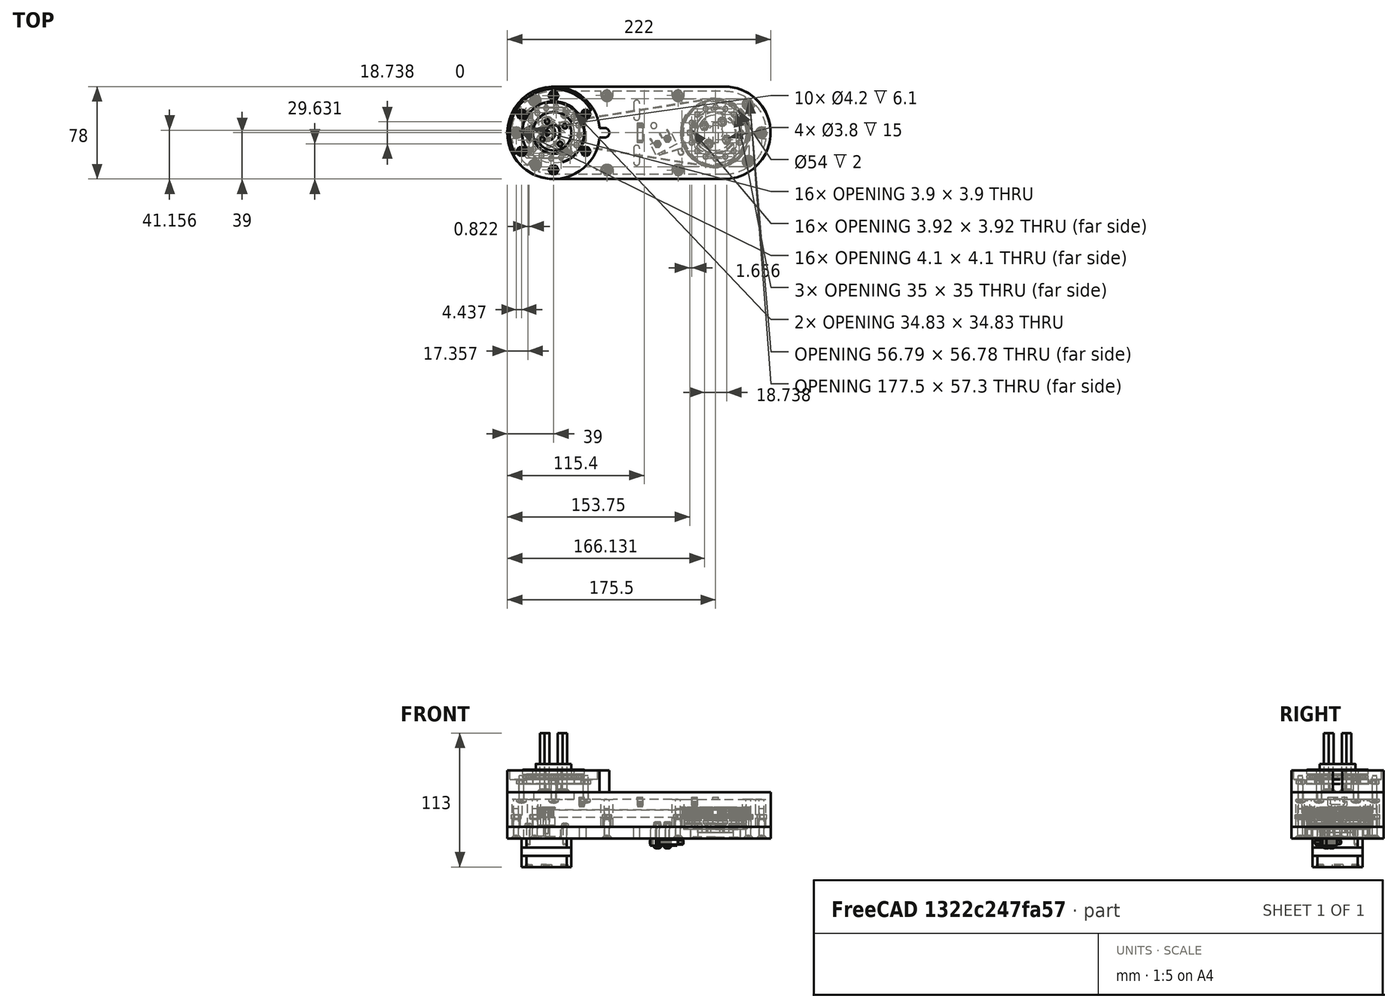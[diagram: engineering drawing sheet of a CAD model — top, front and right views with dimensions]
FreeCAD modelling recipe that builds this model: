
FCSTD DOCUMENT  (FreeCAD 0.19R)
Label: Arm2_a2p
License: All rights reserved
LicenseURL: http://en.wikipedia.org/wiki/All_rights_reserved
objects: Part::FeaturePython×66, App::FeaturePython×48, Spreadsheet::Sheet×2, App::DocumentObjectGroup×1
note: 66 computed .brp shape members not serialized (recipe doc carries the construction recipe); baked Part::Feature solids carry a one-line shape summary decoded from their .brp

FEATURE [Part::FeaturePython] b_Arm2_cover_modified_001_  label="Arm2_cover_modified_001"  # a2plus imported part (geometry in sourceFile) (typed FeaturePython)
  Placement = pos=(0,0,0) rot=(1,0,0;1.5708rad)
  a2p_Version = V0.1
  fixedPosition = true
  objectType = a2pPart
  sourceFile = ./Arm2_cover_modified.FCStd
  subassemblyImport = false
  timeLastImport = 1.62057e+09
  updateColors = true
FEATURE [Part::FeaturePython] b_Thrust_bearing_511071_001_  label="Thrust_bearing_511071_001"  # a2plus imported part (geometry in sourceFile) (typed FeaturePython)
  Placement = pos=(-7.5,3.014e-12,8) rot=(1,0,0;1.5708rad)
  a2p_Version = V0.1
  fixedPosition = false
  objectType = a2pPart
  sourceFile = ./Thrust_bearing_51107.step
  subassemblyImport = false
  timeLastImport = 1.62049e+09
  updateColors = true
FEATURE [App::FeaturePython] circularEdge_002  label="circularEdge_002__Arm2_cover_modified_001"  # a2plus constraint (typed FeaturePython)
  Object1 = b_Thrust_bearing_511071_001_
  Object2 = b_Arm2_cover_modified_001_
  ParentTreeObject = -> b_Thrust_bearing_511071_001_
  SubElement1 = Edge18
  SubElement2 = Edge329
  Suppressed = false
  Type = circularEdge
  directionConstraint = 1
  lockRotation = false
  offset = 0
FEATURE [App::FeaturePython] circularEdge_002_mirror  label="circularEdge_002__Thrust_bearing_511071_001"  # a2plus constraint (typed FeaturePython)
  Object1 = b_Thrust_bearing_511071_001_
  Object2 = b_Arm2_cover_modified_001_
  ParentTreeObject = -> b_Arm2_cover_modified_001_
  SubElement1 = Edge18
  SubElement2 = Edge329
  Suppressed = false
  Type = circularEdge
  directionConstraint = 1
  lockRotation = false
  offset = 0
FEATURE [Part::FeaturePython] b_Stepper_NEMA17_l24mm_shaft_20mm1_001_  label="Stepper_NEMA17_l24mm_shaft_20mm1_001"  # a2plus imported part (geometry in sourceFile) (typed FeaturePython)
  Placement = pos=(-150,-3.93946e-07,-24) rot=(1,0,0;1.5708rad)
  a2p_Version = V0.1
  fixedPosition = false
  objectType = a2pPart
  sourceFile = ./Stepper_NEMA17_l24mm_shaft_20mm.step
  subassemblyImport = false
  timeLastImport = 1.62058e+09
  updateColors = true
FEATURE [App::FeaturePython] circularEdge_004  label="circularEdge_004__Arm2_cover_modified_001"  # a2plus constraint (typed FeaturePython)
  Object1 = b_Stepper_NEMA17_l24mm_shaft_20mm1_001_
  Object2 = b_Arm2_cover_modified_001_
  ParentTreeObject = -> b_Stepper_NEMA17_l24mm_shaft_20mm1_001_
  SubElement1 = Edge95
  SubElement2 = Edge24
  Suppressed = false
  Type = circularEdge
  directionConstraint = 0
  lockRotation = false
  offset = 0
FEATURE [App::FeaturePython] circularEdge_004_mirror  label="circularEdge_004__Stepper_NEMA17_l24mm_shaft_20mm1_001"  # a2plus constraint (typed FeaturePython)
  Object1 = b_Stepper_NEMA17_l24mm_shaft_20mm1_001_
  Object2 = b_Arm2_cover_modified_001_
  ParentTreeObject = -> b_Arm2_cover_modified_001_
  SubElement1 = Edge95
  SubElement2 = Edge24
  Suppressed = false
  Type = circularEdge
  directionConstraint = 0
  lockRotation = false
  offset = 0
FEATURE [App::FeaturePython] axisCoincident_001  label="axisCoincident_001__Arm2_cover_modified_001"  # a2plus constraint (typed FeaturePython)
  Object1 = b_Stepper_NEMA17_l24mm_shaft_20mm1_001_
  Object2 = b_Arm2_cover_modified_001_
  ParentTreeObject = -> b_Stepper_NEMA17_l24mm_shaft_20mm1_001_
  SubElement1 = Face40
  SubElement2 = Face44
  Suppressed = false
  Type = axial
  directionConstraint = 0
  lockRotation = false
FEATURE [App::FeaturePython] axisCoincident_001_mirror  label="axisCoincident_001__Stepper_NEMA17_l24mm_shaft_20mm1_001"  # a2plus constraint (typed FeaturePython)
  Object1 = b_Stepper_NEMA17_l24mm_shaft_20mm1_001_
  Object2 = b_Arm2_cover_modified_001_
  ParentTreeObject = -> b_Arm2_cover_modified_001_
  SubElement1 = Face40
  SubElement2 = Face44
  Suppressed = false
  Type = axial
  directionConstraint = 0
  lockRotation = false
FEATURE [Part::FeaturePython] b_Pulley_GT2_20t1_001_  label="Pulley_GT2-20t1_001"  # a2plus imported part (geometry in sourceFile) (typed FeaturePython)
  Placement = pos=(-209.577,47.8545,-1.09998) rot=(-0.402665,-0.647248,0.647248;2.37599rad)
  a2p_Version = V0.1
  fixedPosition = false
  objectType = a2pPart
  sourceFile = ./Pulley_GT2-20t.step
  subassemblyImport = false
  timeLastImport = 1.61956e+09
  updateColors = true
FEATURE [App::FeaturePython] axisCoincident_002  label="axisCoincident_002__Stepper_NEMA17_l24mm_shaft_20mm1_001"  # a2plus constraint (typed FeaturePython)
  Object1 = b_Pulley_GT2_20t1_001_
  Object2 = b_Stepper_NEMA17_l24mm_shaft_20mm1_001_
  ParentTreeObject = -> b_Pulley_GT2_20t1_001_
  SubElement1 = Face190
  SubElement2 = Face31
  Suppressed = false
  Type = axial
  directionConstraint = 1
  lockRotation = false
FEATURE [App::FeaturePython] axisCoincident_002_mirror  label="axisCoincident_002__Pulley_GT2-20t1_001"  # a2plus constraint (typed FeaturePython)
  Object1 = b_Pulley_GT2_20t1_001_
  Object2 = b_Stepper_NEMA17_l24mm_shaft_20mm1_001_
  ParentTreeObject = -> b_Stepper_NEMA17_l24mm_shaft_20mm1_001_
  SubElement1 = Face190
  SubElement2 = Face31
  Suppressed = false
  Type = axial
  directionConstraint = 1
  lockRotation = false
FEATURE [Part::FeaturePython] b_Belt_GT2_400mm_20_901_001_  label="Belt_GT2_400mm_20-901_001"  # a2plus imported part (geometry in sourceFile) (typed FeaturePython)
  Placement = pos=(-7.5,7.81778e-08,24.2) rot=(-1,0,0;1.5708rad)
  a2p_Version = V0.1
  fixedPosition = false
  objectType = a2pPart
  sourceFile = ./Belt_GT2_400mm_20-90.step
  subassemblyImport = false
  timeLastImport = 1.62058e+09
  updateColors = true
FEATURE [App::FeaturePython] axisCoincident_003  label="axisCoincident_003__Pulley_GT2-20t1_001"  # a2plus constraint (typed FeaturePython)
  Object1 = b_Belt_GT2_400mm_20_901_001_
  Object2 = b_Pulley_GT2_20t1_001_
  ParentTreeObject = -> b_Belt_GT2_400mm_20_901_001_
  SubElement1 = Face11
  SubElement2 = Face187
  Suppressed = false
  Type = axial
  directionConstraint = 0
  lockRotation = false
FEATURE [App::FeaturePython] axisCoincident_003_mirror  label="axisCoincident_003__Belt_GT2_400mm_20-901_001"  # a2plus constraint (typed FeaturePython)
  Object1 = b_Belt_GT2_400mm_20_901_001_
  Object2 = b_Pulley_GT2_20t1_001_
  ParentTreeObject = -> b_Pulley_GT2_20t1_001_
  SubElement1 = Face11
  SubElement2 = Face187
  Suppressed = false
  Type = axial
  directionConstraint = 0
  lockRotation = false
FEATURE [Part::FeaturePython] b_Arm2_modified_001_  label="Arm2_modified_001"  # a2plus imported part (geometry in sourceFile) (typed FeaturePython)
  Placement = pos=(0,-4.78538e-07,39) rot=(-1,0,0;1.5708rad)
  a2p_Version = V0.1
  fixedPosition = false
  objectType = a2pPart
  sourceFile = ./Arm2_modified.FCStd
  subassemblyImport = false
  timeLastImport = 1.62049e+09
  updateColors = true
FEATURE [Part::FeaturePython] b_Cable_routing_clamp_16_8_4_5_001_  label="Cable_routing_clamp_16*8*4.5_001"  # a2plus imported part (geometry in sourceFile) (typed FeaturePython)
  Placement = pos=(-122.4,-8.1,27) rot=(0.57735,0.57735,0.57735;2.0944rad)
  a2p_Version = V0.1
  fixedPosition = false
  objectType = a2pPart
  sourceFile = ./Cable_routing_clamp_16*8*4.5.FCStd
  subassemblyImport = false
  timeLastImport = 1.62049e+09
  updateColors = true
FEATURE [App::FeaturePython] circularEdge_006  label="circularEdge_006__Arm2_cover_modified_001"  # a2plus constraint (typed FeaturePython)
  Object1 = b_Arm2_modified_001_
  Object2 = b_Arm2_cover_modified_001_
  ParentTreeObject = -> b_Arm2_modified_001_
  SubElement1 = Edge125
  SubElement2 = Edge114
  Suppressed = false
  Type = circularEdge
  directionConstraint = 0
  lockRotation = true
  offset = 0
FEATURE [App::FeaturePython] circularEdge_006_mirror  label="circularEdge_006__Arm2_modified_001"  # a2plus constraint (typed FeaturePython)
  Object1 = b_Arm2_modified_001_
  Object2 = b_Arm2_cover_modified_001_
  ParentTreeObject = -> b_Arm2_cover_modified_001_
  SubElement1 = Edge125
  SubElement2 = Edge114
  Suppressed = false
  Type = circularEdge
  directionConstraint = 0
  lockRotation = true
  offset = 0
FEATURE [App::FeaturePython] planeCoincident_002  label="planeCoincident_002__Arm2_modified_001"  # a2plus constraint (typed FeaturePython)
  Object1 = b_Cable_routing_clamp_16_8_4_5_001_
  Object2 = b_Arm2_modified_001_
  ParentTreeObject = -> b_Cable_routing_clamp_16_8_4_5_001_
  SubElement1 = Face9
  SubElement2 = Face77
  Suppressed = false
  Type = plane
  directionConstraint = 1
  offset = 0
FEATURE [App::FeaturePython] planeCoincident_002_mirror  label="planeCoincident_002__Cable_routing_clamp_16*8*4.5_001"  # a2plus constraint (typed FeaturePython)
  Object1 = b_Cable_routing_clamp_16_8_4_5_001_
  Object2 = b_Arm2_modified_001_
  ParentTreeObject = -> b_Arm2_modified_001_
  SubElement1 = Face9
  SubElement2 = Face77
  Suppressed = false
  Type = plane
  directionConstraint = 1
  offset = 0
FEATURE [App::FeaturePython] planeCoincident_003  label="planeCoincident_003__Arm2_modified_001"  # a2plus constraint (typed FeaturePython)
  Object1 = b_Cable_routing_clamp_16_8_4_5_001_
  Object2 = b_Arm2_modified_001_
  ParentTreeObject = -> b_Cable_routing_clamp_16_8_4_5_001_
  SubElement1 = Face5
  SubElement2 = Face166
  Suppressed = false
  Type = plane
  directionConstraint = 0
  offset = 0
FEATURE [App::FeaturePython] planeCoincident_003_mirror  label="planeCoincident_003__Cable_routing_clamp_16*8*4.5_001"  # a2plus constraint (typed FeaturePython)
  Object1 = b_Cable_routing_clamp_16_8_4_5_001_
  Object2 = b_Arm2_modified_001_
  ParentTreeObject = -> b_Arm2_modified_001_
  SubElement1 = Face5
  SubElement2 = Face166
  Suppressed = false
  Type = plane
  directionConstraint = 0
  offset = 0
FEATURE [App::FeaturePython] planeCoincident_004  label="planeCoincident_004__Arm2_modified_001"  # a2plus constraint (typed FeaturePython)
  Object1 = b_Cable_routing_clamp_16_8_4_5_001_
  Object2 = b_Arm2_modified_001_
  ParentTreeObject = -> b_Cable_routing_clamp_16_8_4_5_001_
  SubElement1 = Face24
  SubElement2 = Face76
  Suppressed = false
  Type = plane
  directionConstraint = 0
  offset = 0
FEATURE [App::FeaturePython] planeCoincident_004_mirror  label="planeCoincident_004__Cable_routing_clamp_16*8*4.5_001"  # a2plus constraint (typed FeaturePython)
  Object1 = b_Cable_routing_clamp_16_8_4_5_001_
  Object2 = b_Arm2_modified_001_
  ParentTreeObject = -> b_Arm2_modified_001_
  SubElement1 = Face24
  SubElement2 = Face76
  Suppressed = false
  Type = plane
  directionConstraint = 0
  offset = 0
FEATURE [Part::FeaturePython] b_Cable_routing_clamp_16_8_4_5_001_001  label="Cable_routing_clamp_16*8*4.5_002"  # a2plus imported part (geometry in sourceFile) (typed FeaturePython)
  Placement = pos=(-73.4,-8.1,27) rot=(0.57735,0.57735,0.57735;2.0944rad)
  a2p_Version = V0.1
  fixedPosition = false
  objectType = a2pPart
  sourceFile = ./Cable_routing_clamp_16*8*4.5.FCStd
  subassemblyImport = false
  timeLastImport = 1.62049e+09
  updateColors = true
FEATURE [App::FeaturePython] planeCoincident_005  label="planeCoincident_005__Arm2_modified_001"  # a2plus constraint (typed FeaturePython)
  Object1 = b_Cable_routing_clamp_16_8_4_5_001_001
  Object2 = b_Arm2_modified_001_
  ParentTreeObject = -> b_Cable_routing_clamp_16_8_4_5_001_001
  SubElement1 = Face24
  SubElement2 = Face82
  Suppressed = false
  Type = plane
  directionConstraint = 0
  offset = 0
FEATURE [App::FeaturePython] planeCoincident_005_mirror  label="planeCoincident_005__Cable_routing_clamp_16*8*4.5_002"  # a2plus constraint (typed FeaturePython)
  Object1 = b_Cable_routing_clamp_16_8_4_5_001_001
  Object2 = b_Arm2_modified_001_
  ParentTreeObject = -> b_Arm2_modified_001_
  SubElement1 = Face24
  SubElement2 = Face82
  Suppressed = false
  Type = plane
  directionConstraint = 0
  offset = 0
FEATURE [App::FeaturePython] planeCoincident_006  label="planeCoincident_006__Arm2_modified_001"  # a2plus constraint (typed FeaturePython)
  Object1 = b_Cable_routing_clamp_16_8_4_5_001_001
  Object2 = b_Arm2_modified_001_
  ParentTreeObject = -> b_Cable_routing_clamp_16_8_4_5_001_001
  SubElement1 = Face9
  SubElement2 = Face83
  Suppressed = false
  Type = plane
  directionConstraint = 1
  offset = 0
FEATURE [App::FeaturePython] planeCoincident_006_mirror  label="planeCoincident_006__Cable_routing_clamp_16*8*4.5_002"  # a2plus constraint (typed FeaturePython)
  Object1 = b_Cable_routing_clamp_16_8_4_5_001_001
  Object2 = b_Arm2_modified_001_
  ParentTreeObject = -> b_Arm2_modified_001_
  SubElement1 = Face9
  SubElement2 = Face83
  Suppressed = false
  Type = plane
  directionConstraint = 1
  offset = 0
FEATURE [App::FeaturePython] planeCoincident_007  label="planeCoincident_007__Cable_routing_clamp_16*8*4.5_001"  # a2plus constraint (typed FeaturePython)
  Object1 = b_Cable_routing_clamp_16_8_4_5_001_001
  Object2 = b_Cable_routing_clamp_16_8_4_5_001_
  ParentTreeObject = -> b_Cable_routing_clamp_16_8_4_5_001_001
  SubElement1 = Face13
  SubElement2 = Face13
  Suppressed = false
  Type = plane
  directionConstraint = 0
  offset = 0
FEATURE [App::FeaturePython] planeCoincident_007_mirror  label="planeCoincident_007__Cable_routing_clamp_16*8*4.5_002"  # a2plus constraint (typed FeaturePython)
  Object1 = b_Cable_routing_clamp_16_8_4_5_001_001
  Object2 = b_Cable_routing_clamp_16_8_4_5_001_
  ParentTreeObject = -> b_Cable_routing_clamp_16_8_4_5_001_
  SubElement1 = Face13
  SubElement2 = Face13
  Suppressed = false
  Type = plane
  directionConstraint = 0
  offset = 0
FEATURE [Part::FeaturePython] b_Cable_routing_clamp_16_8_4_5_001_002  label="Cable_routing_clamp_16*8*4.5_003"  # a2plus imported part (geometry in sourceFile) (typed FeaturePython)
  Placement = pos=(-27.4,-8.1,27) rot=(0.57735,0.57735,0.57735;2.0944rad)
  a2p_Version = V0.1
  fixedPosition = false
  objectType = a2pPart
  sourceFile = ./Cable_routing_clamp_16*8*4.5.FCStd
  subassemblyImport = false
  timeLastImport = 1.62049e+09
  updateColors = true
FEATURE [App::FeaturePython] planeCoincident_008  label="planeCoincident_008__Arm2_modified_001"  # a2plus constraint (typed FeaturePython)
  Object1 = b_Cable_routing_clamp_16_8_4_5_001_002
  Object2 = b_Arm2_modified_001_
  ParentTreeObject = -> b_Cable_routing_clamp_16_8_4_5_001_002
  SubElement1 = Face9
  SubElement2 = Face87
  Suppressed = false
  Type = plane
  directionConstraint = 1
  offset = 0
FEATURE [App::FeaturePython] planeCoincident_008_mirror  label="planeCoincident_008__Cable_routing_clamp_16*8*4.5_003"  # a2plus constraint (typed FeaturePython)
  Object1 = b_Cable_routing_clamp_16_8_4_5_001_002
  Object2 = b_Arm2_modified_001_
  ParentTreeObject = -> b_Arm2_modified_001_
  SubElement1 = Face9
  SubElement2 = Face87
  Suppressed = false
  Type = plane
  directionConstraint = 1
  offset = 0
FEATURE [App::FeaturePython] planeCoincident_009  label="planeCoincident_009__Arm2_modified_001"  # a2plus constraint (typed FeaturePython)
  Object1 = b_Cable_routing_clamp_16_8_4_5_001_002
  Object2 = b_Arm2_modified_001_
  ParentTreeObject = -> b_Cable_routing_clamp_16_8_4_5_001_002
  SubElement1 = Face24
  SubElement2 = Face86
  Suppressed = false
  Type = plane
  directionConstraint = 0
  offset = 0
FEATURE [App::FeaturePython] planeCoincident_009_mirror  label="planeCoincident_009__Cable_routing_clamp_16*8*4.5_003"  # a2plus constraint (typed FeaturePython)
  Object1 = b_Cable_routing_clamp_16_8_4_5_001_002
  Object2 = b_Arm2_modified_001_
  ParentTreeObject = -> b_Arm2_modified_001_
  SubElement1 = Face24
  SubElement2 = Face86
  Suppressed = false
  Type = plane
  directionConstraint = 0
  offset = 0
FEATURE [App::FeaturePython] planeCoincident_010  label="planeCoincident_010__Cable_routing_clamp_16*8*4.5_001"  # a2plus constraint (typed FeaturePython)
  Object1 = b_Cable_routing_clamp_16_8_4_5_001_002
  Object2 = b_Cable_routing_clamp_16_8_4_5_001_
  ParentTreeObject = -> b_Cable_routing_clamp_16_8_4_5_001_002
  SubElement1 = Face13
  SubElement2 = Face13
  Suppressed = false
  Type = plane
  directionConstraint = 0
  offset = 0
FEATURE [App::FeaturePython] planeCoincident_010_mirror  label="planeCoincident_010__Cable_routing_clamp_16*8*4.5_003"  # a2plus constraint (typed FeaturePython)
  Object1 = b_Cable_routing_clamp_16_8_4_5_001_002
  Object2 = b_Cable_routing_clamp_16_8_4_5_001_
  ParentTreeObject = -> b_Cable_routing_clamp_16_8_4_5_001_
  SubElement1 = Face13
  SubElement2 = Face13
  Suppressed = false
  Type = plane
  directionConstraint = 0
  offset = 0
FEATURE [Part::FeaturePython] b_J2_coupler_modified_001_  label="J2_coupler_modified_001"  # a2plus imported part (geometry in sourceFile) (typed FeaturePython)
  Placement = pos=(-144,7.32498e-07,39) rot=(0.377965,0.654654,0.654654;2.41886rad)
  a2p_Version = V0.1
  fixedPosition = false
  objectType = a2pPart
  sourceFile = ./J2_coupler_modified.FCStd
  subassemblyImport = false
  timeLastImport = 1.62049e+09
  updateColors = true
FEATURE [App::FeaturePython] circularEdge_007  label="circularEdge_007__Arm2_modified_001"  # a2plus constraint (typed FeaturePython)
  Object1 = b_J2_coupler_modified_001_
  Object2 = b_Arm2_modified_001_
  ParentTreeObject = -> b_J2_coupler_modified_001_
  SubElement1 = Edge11
  SubElement2 = Edge345
  Suppressed = false
  Type = circularEdge
  directionConstraint = 1
  lockRotation = false
  offset = 0
FEATURE [App::FeaturePython] circularEdge_007_mirror  label="circularEdge_007__J2_coupler_modified_001"  # a2plus constraint (typed FeaturePython)
  Object1 = b_J2_coupler_modified_001_
  Object2 = b_Arm2_modified_001_
  ParentTreeObject = -> b_Arm2_modified_001_
  SubElement1 = Edge11
  SubElement2 = Edge345
  Suppressed = false
  Type = circularEdge
  directionConstraint = 1
  lockRotation = false
  offset = 0
FEATURE [App::FeaturePython] axisCoincident_004  label="axisCoincident_004__Arm2_modified_001"  # a2plus constraint (typed FeaturePython)
  Object1 = b_J2_coupler_modified_001_
  Object2 = b_Arm2_modified_001_
  ParentTreeObject = -> b_J2_coupler_modified_001_
  SubElement1 = Edge138
  SubElement2 = Edge327
  Suppressed = false
  Type = axial
  directionConstraint = 1
  lockRotation = false
FEATURE [App::FeaturePython] axisCoincident_004_mirror  label="axisCoincident_004__J2_coupler_modified_001"  # a2plus constraint (typed FeaturePython)
  Object1 = b_J2_coupler_modified_001_
  Object2 = b_Arm2_modified_001_
  ParentTreeObject = -> b_Arm2_modified_001_
  SubElement1 = Edge138
  SubElement2 = Edge327
  Suppressed = false
  Type = axial
  directionConstraint = 1
  lockRotation = false
FEATURE [Part::FeaturePython] b_Thrust_bearing_511071_001_001  label="Thrust_bearing_511071_002"  # a2plus imported part (geometry in sourceFile) (typed FeaturePython)
  Placement = pos=(-144,8.98781e-07,58) rot=(-0.978852,-0.144653,0.144653;1.59217rad)
  a2p_Version = V0.1
  fixedPosition = false
  objectType = a2pPart
  sourceFile = ./Thrust_bearing_51107.step
  subassemblyImport = false
  timeLastImport = 1.62049e+09
  updateColors = true
FEATURE [App::FeaturePython] planeCoincident_014  label="planeCoincident_014__J2_coupler_modified_001"  # a2plus constraint (typed FeaturePython)
  Object1 = b_Thrust_bearing_511071_001_001
  Object2 = b_J2_coupler_modified_001_
  ParentTreeObject = -> b_Thrust_bearing_511071_001_001
  SubElement1 = Face13
  SubElement2 = Face99
  Suppressed = false
  Type = plane
  directionConstraint = 1
  offset = 0
FEATURE [App::FeaturePython] planeCoincident_014_mirror  label="planeCoincident_014__Thrust_bearing_511071_002"  # a2plus constraint (typed FeaturePython)
  Object1 = b_Thrust_bearing_511071_001_001
  Object2 = b_J2_coupler_modified_001_
  ParentTreeObject = -> b_J2_coupler_modified_001_
  SubElement1 = Face13
  SubElement2 = Face99
  Suppressed = false
  Type = plane
  directionConstraint = 1
  offset = 0
FEATURE [App::FeaturePython] axisCoincident_005  label="axisCoincident_005__J2_coupler_modified_001"  # a2plus constraint (typed FeaturePython)
  Object1 = b_Thrust_bearing_511071_001_001
  Object2 = b_J2_coupler_modified_001_
  ParentTreeObject = -> b_Thrust_bearing_511071_001_001
  SubElement1 = Face2
  SubElement2 = Face88
  Suppressed = false
  Type = axial
  directionConstraint = 0
  lockRotation = false
FEATURE [App::FeaturePython] axisCoincident_005_mirror  label="axisCoincident_005__Thrust_bearing_511071_002"  # a2plus constraint (typed FeaturePython)
  Object1 = b_Thrust_bearing_511071_001_001
  Object2 = b_J2_coupler_modified_001_
  ParentTreeObject = -> b_J2_coupler_modified_001_
  SubElement1 = Face2
  SubElement2 = Face88
  Suppressed = false
  Type = axial
  directionConstraint = 0
  lockRotation = false
FEATURE [Part::FeaturePython] b_Switch_endstop1_001_  label="Switch_endstop1_001"  # a2plus imported part (geometry in sourceFile) (typed FeaturePython)
  Placement = pos=(-51.2411,-9.55473,-7.65812e-08) rot=(0.970296,0.241922,0;3.14159rad)
  a2p_Version = V0.1
  fixedPosition = false
  objectType = a2pPart
  sourceFile = ./Switch_endstop.step
  subassemblyImport = false
  timeLastImport = 1598970250
  updateColors = true
FEATURE [App::FeaturePython] circularEdge_008  label="circularEdge_008__Arm2_cover_modified_001"  # a2plus constraint (typed FeaturePython)
  Object1 = b_Switch_endstop1_001_
  Object2 = b_Arm2_cover_modified_001_
  ParentTreeObject = -> b_Switch_endstop1_001_
  SubElement1 = Edge39
  SubElement2 = Edge71
  Suppressed = false
  Type = circularEdge
  directionConstraint = 1
  lockRotation = false
  offset = 0
FEATURE [App::FeaturePython] circularEdge_008_mirror  label="circularEdge_008__Switch_endstop1_001"  # a2plus constraint (typed FeaturePython)
  Object1 = b_Switch_endstop1_001_
  Object2 = b_Arm2_cover_modified_001_
  ParentTreeObject = -> b_Arm2_cover_modified_001_
  SubElement1 = Edge39
  SubElement2 = Edge71
  Suppressed = false
  Type = circularEdge
  directionConstraint = 1
  lockRotation = false
  offset = 0
FEATURE [App::FeaturePython] axisCoincident_006  label="axisCoincident_006__Arm2_cover_modified_001"  # a2plus constraint (typed FeaturePython)
  Object1 = b_Switch_endstop1_001_
  Object2 = b_Arm2_cover_modified_001_
  ParentTreeObject = -> b_Switch_endstop1_001_
  SubElement1 = Face10
  SubElement2 = Face64
  Suppressed = false
  Type = axial
  directionConstraint = 1
  lockRotation = false
FEATURE [App::FeaturePython] axisCoincident_006_mirror  label="axisCoincident_006__Switch_endstop1_001"  # a2plus constraint (typed FeaturePython)
  Object1 = b_Switch_endstop1_001_
  Object2 = b_Arm2_cover_modified_001_
  ParentTreeObject = -> b_Arm2_cover_modified_001_
  SubElement1 = Face10
  SubElement2 = Face64
  Suppressed = false
  Type = axial
  directionConstraint = 1
  lockRotation = false
FEATURE [Part::FeaturePython] Nut  label="M4-Nut"  # Fasteners workbench fastener (typed FeaturePython)
  Placement = pos=(-99,31.5,20) rot=(1,0,0;3.14159rad)
  baseObject = -> b_Arm2_modified_001_ [Edge461]
  diameter = 6
  invert = true
  matchOuter = false
  offset = 0
  thread = false
  type = 7
FEATURE [Part::FeaturePython] Nut001  label="M4-Nut001"  # Fasteners workbench fastener (typed FeaturePython)
  Placement = pos=(-159.75,27.2798,20) rot=(1,0,0;3.14159rad)
  baseObject = -> b_Arm2_modified_001_ [Edge485]
  diameter = 6
  invert = false
  matchOuter = false
  offset = 0
  thread = false
  type = 7
FEATURE [Part::FeaturePython] Nut002  label="M4-Nut002"  # Fasteners workbench fastener (typed FeaturePython)
  Placement = pos=(-175.5,-1.65013e-07,20) rot=(1,0,0;3.14159rad)
  baseObject = -> b_Arm2_modified_001_ [Edge509]
  diameter = 6
  invert = false
  matchOuter = false
  offset = 0
  thread = false
  type = 7
FEATURE [Part::FeaturePython] Nut003  label="M4-Nut003"  # Fasteners workbench fastener (typed FeaturePython)
  Placement = pos=(-159.75,-27.2798,20) rot=(1,0,0;3.14159rad)
  baseObject = -> b_Arm2_modified_001_ [Edge535]
  diameter = 6
  invert = false
  matchOuter = false
  offset = 0
  thread = false
  type = 7
FEATURE [Part::FeaturePython] Nut004  label="M4-Nut004"  # Fasteners workbench fastener (typed FeaturePython)
  Placement = pos=(-99,-31.5,20) rot=(1,0,0;3.14159rad)
  baseObject = -> b_Arm2_modified_001_ [Edge546]
  diameter = 6
  invert = false
  matchOuter = false
  offset = 0
  thread = false
  type = 7
FEATURE [Part::FeaturePython] Nut005  label="M4-Nut005"  # Fasteners workbench fastener (typed FeaturePython)
  Placement = pos=(-39,-31.5,20) rot=(1,0,0;3.14159rad)
  baseObject = -> b_Arm2_modified_001_ [Edge520]
  diameter = 6
  invert = false
  matchOuter = false
  offset = 0
  thread = false
  type = 7
FEATURE [Part::FeaturePython] Nut006  label="M4-Nut006"  # Fasteners workbench fastener (typed FeaturePython)
  Placement = pos=(20.2478,-24.1304,20) rot=(1,0,0;3.14159rad)
  baseObject = -> b_Arm2_modified_001_ [Edge497]
  diameter = 6
  invert = false
  matchOuter = false
  offset = 0
  thread = false
  type = 7
FEATURE [Part::FeaturePython] Nut007  label="M4-Nut007"  # Fasteners workbench fastener (typed FeaturePython)
  Placement = pos=(31.5,-1.65013e-07,20) rot=(1,0,0;3.14159rad)
  baseObject = -> b_Arm2_modified_001_ [Edge469]
  diameter = 6
  invert = false
  matchOuter = false
  offset = 0
  thread = false
  type = 7
FEATURE [Part::FeaturePython] Nut008  label="M4-Nut008"  # Fasteners workbench fastener (typed FeaturePython)
  Placement = pos=(20.2478,24.1304,20) rot=(1,0,0;3.14159rad)
  baseObject = -> b_Arm2_modified_001_ [Edge439]
  diameter = 6
  invert = false
  matchOuter = false
  offset = 0
  thread = false
  type = 7
FEATURE [Part::FeaturePython] Nut009  label="M4-Nut009"  # Fasteners workbench fastener (typed FeaturePython)
  Placement = pos=(-39,31.5,20) rot=(1,0,0;3.14159rad)
  baseObject = -> b_Arm2_modified_001_ [Edge4]
  diameter = 6
  invert = true
  matchOuter = false
  offset = 0
  thread = false
  type = 7
FEATURE [Part::FeaturePython] Nut010  label="M4-Nut010"  # Fasteners workbench fastener (typed FeaturePython)
  Placement = pos=(-116.937,15.625,46) rot=(0,0,1;0rad)
  baseObject = -> b_J2_coupler_modified_001_ [Edge56]
  diameter = 6
  invert = false
  matchOuter = false
  offset = 0
  thread = false
  type = 7
FEATURE [Part::FeaturePython] Nut011  label="M4-Nut011"  # Fasteners workbench fastener (typed FeaturePython)
  Placement = pos=(-144,31.25,46) rot=(0,0,1;0rad)
  baseObject = -> b_J2_coupler_modified_001_ [Edge60]
  diameter = 6
  invert = false
  matchOuter = false
  offset = 0
  thread = false
  type = 7
FEATURE [Part::FeaturePython] Nut012  label="M4-Nut012"  # Fasteners workbench fastener (typed FeaturePython)
  Placement = pos=(-171.063,15.625,46) rot=(0,0,1;0rad)
  baseObject = -> b_J2_coupler_modified_001_ [Edge64]
  diameter = 6
  invert = false
  matchOuter = false
  offset = 0
  thread = false
  type = 7
FEATURE [Part::FeaturePython] Nut013  label="M4-Nut013"  # Fasteners workbench fastener (typed FeaturePython)
  Placement = pos=(-171.063,-15.625,46) rot=(0,0,1;0rad)
  baseObject = -> b_J2_coupler_modified_001_ [Edge44]
  diameter = 6
  invert = false
  matchOuter = false
  offset = 0
  thread = false
  type = 7
FEATURE [Part::FeaturePython] Nut014  label="M4-Nut014"  # Fasteners workbench fastener (typed FeaturePython)
  Placement = pos=(-144,-31.25,46) rot=(0,0,1;0rad)
  baseObject = -> b_J2_coupler_modified_001_ [Edge48]
  diameter = 6
  invert = false
  matchOuter = false
  offset = 0
  thread = false
  type = 7
FEATURE [Part::FeaturePython] Nut015  label="M4-Nut015"  # Fasteners workbench fastener (typed FeaturePython)
  Placement = pos=(-116.937,-15.625,46) rot=(0,0,1;0rad)
  baseObject = -> b_J2_coupler_modified_001_ [Edge52]
  diameter = 6
  invert = false
  matchOuter = false
  offset = 0
  thread = false
  type = 7
FEATURE [Part::FeaturePython] Screw  label="M4x25-Screw"  # Fasteners workbench fastener (typed FeaturePython)
  Placement = pos=(-99,31.5,-9e-15) rot=(1,0,0;3.14159rad)
  baseObject = -> b_Arm2_cover_modified_001_ [Edge34]
  diameter = 6
  invert = false
  length = 8
  lengthCustom = 25
  matchOuter = false
  offset = 0
  thread = false
  type = 35
FEATURE [Part::FeaturePython] Screw001  label="M4x25-Screw001"  # Fasteners workbench fastener (typed FeaturePython)
  Placement = pos=(-39,31.5,-9e-15) rot=(1,0,0;3.14159rad)
  baseObject = -> b_Arm2_cover_modified_001_ [Edge62]
  diameter = 6
  invert = false
  length = 8
  lengthCustom = 25
  matchOuter = false
  offset = 0
  thread = false
  type = 35
FEATURE [Part::FeaturePython] Screw002  label="M4x25-Screw002"  # Fasteners workbench fastener (typed FeaturePython)
  Placement = pos=(20.2478,24.1304,-7e-15) rot=(1,0,0;3.14159rad)
  baseObject = -> b_Arm2_cover_modified_001_ [Edge66]
  diameter = 6
  invert = false
  length = 8
  lengthCustom = 25
  matchOuter = false
  offset = 0
  thread = false
  type = 35
FEATURE [Part::FeaturePython] Screw003  label="M4x25-Screw003"  # Fasteners workbench fastener (typed FeaturePython)
  Placement = pos=(31.5,0,-2e-15) rot=(1,0,0;3.14159rad)
  baseObject = -> b_Arm2_cover_modified_001_ [Edge76]
  diameter = 6
  invert = false
  length = 8
  lengthCustom = 25
  matchOuter = false
  offset = 0
  thread = false
  type = 35
FEATURE [Part::FeaturePython] Screw004  label="M4x25-Screw004"  # Fasteners workbench fastener (typed FeaturePython)
  Placement = pos=(20.2478,-24.1304,4e-15) rot=(1,0,0;3.14159rad)
  baseObject = -> b_Arm2_cover_modified_001_ [Edge78]
  diameter = 6
  invert = false
  length = 8
  lengthCustom = 25
  matchOuter = false
  offset = 0
  thread = false
  type = 35
FEATURE [Part::FeaturePython] Screw005  label="M4x25-Screw005"  # Fasteners workbench fastener (typed FeaturePython)
  Placement = pos=(-39,-31.5,5e-15) rot=(1,0,0;3.14159rad)
  baseObject = -> b_Arm2_cover_modified_001_ [Edge72]
  diameter = 6
  invert = false
  length = 8
  lengthCustom = 25
  matchOuter = false
  offset = 0
  thread = false
  type = 35
FEATURE [Part::FeaturePython] Screw006  label="M4x25-Screw006"  # Fasteners workbench fastener (typed FeaturePython)
  Placement = pos=(-99,-31.5,5e-15) rot=(1,0,0;3.14159rad)
  baseObject = -> b_Arm2_cover_modified_001_ [Edge60]
  diameter = 6
  invert = false
  length = 8
  lengthCustom = 25
  matchOuter = false
  offset = 0
  thread = false
  type = 35
FEATURE [Part::FeaturePython] Screw007  label="M4x25-Screw007"  # Fasteners workbench fastener (typed FeaturePython)
  Placement = pos=(-159.75,-27.2798,4e-15) rot=(1,0,0;3.14159rad)
  baseObject = -> b_Arm2_cover_modified_001_ [Edge51]
  diameter = 6
  invert = false
  length = 8
  lengthCustom = 25
  matchOuter = false
  offset = 0
  thread = false
  type = 35
FEATURE [Part::FeaturePython] Screw008  label="M4x25-Screw008"  # Fasteners workbench fastener (typed FeaturePython)
  Placement = pos=(-175.5,-3e-15,-2e-15) rot=(1,0,0;3.14159rad)
  baseObject = -> b_Arm2_cover_modified_001_ [Edge41]
  diameter = 6
  invert = false
  length = 8
  lengthCustom = 25
  matchOuter = false
  offset = 0
  thread = false
  type = 35
FEATURE [Part::FeaturePython] Screw009  label="M4x25-Screw009"  # Fasteners workbench fastener (typed FeaturePython)
  Placement = pos=(-159.75,27.2798,-8e-15) rot=(1,0,0;3.14159rad)
  baseObject = -> b_Arm2_cover_modified_001_ [Edge18]
  diameter = 6
  invert = false
  length = 8
  lengthCustom = 25
  matchOuter = false
  offset = 0
  thread = false
  type = 35
FEATURE [Part::FeaturePython] Screw010  label="M3x20-Screw"  # Fasteners workbench fastener (typed FeaturePython)
  Placement = pos=(-48,-5,-6) rot=(0.882947,0.469472,0;3.14159rad)
  baseObject = -> b_Switch_endstop1_001_ [Edge37]
  diameter = 4
  invert = false
  length = 8
  lengthCustom = 20
  matchOuter = false
  offset = 0
  thread = false
  type = 34
FEATURE [Part::FeaturePython] Screw011  label="M3x20-Screw001"  # Fasteners workbench fastener (typed FeaturePython)
  Placement = pos=(-56.388,-9.45998,-6) rot=(0.882947,0.469472,0;3.14159rad)
  baseObject = -> b_Switch_endstop1_001_ [Edge36]
  diameter = 4
  invert = false
  length = 8
  lengthCustom = 20
  matchOuter = false
  offset = 0
  thread = false
  type = 34
FEATURE [Part::FeaturePython] Nut016  label="M3-Nut"  # Fasteners workbench fastener (typed FeaturePython)
  Placement = pos=(-56.388,-9.45998,10) rot=(0,0,1;0rad)
  baseObject = -> b_Arm2_cover_modified_001_ [Edge143]
  diameter = 1
  invert = false
  matchOuter = false
  offset = 0
  thread = false
  type = 5
FEATURE [Part::FeaturePython] Nut017  label="M3-Nut001"  # Fasteners workbench fastener (typed FeaturePython)
  Placement = pos=(-48,-5,10) rot=(0,0,1;0rad)
  baseObject = -> b_Arm2_cover_modified_001_ [Edge141]
  diameter = 1
  invert = false
  matchOuter = false
  offset = 0
  thread = false
  type = 5
FEATURE [Part::FeaturePython] Screw012  label="M4x50-Screw"  # Fasteners workbench fastener (typed FeaturePython)
  Placement = pos=(-153.526,-5.5,39) rot=(-0.652223,0.758027,0;3.14159rad)
  baseObject = -> b_J2_coupler_modified_001_ [Edge31]
  diameter = 6
  invert = false
  length = 12
  lengthCustom = 50
  matchOuter = false
  offset = 0
  thread = false
  type = 35
FEATURE [Part::FeaturePython] Screw013  label="M4x50-Screw001"  # Fasteners workbench fastener (typed FeaturePython)
  Placement = pos=(-149.5,9.52628,39) rot=(-0.652223,0.758027,0;3.14159rad)
  baseObject = -> b_J2_coupler_modified_001_ [Edge20]
  diameter = 6
  invert = false
  length = 12
  lengthCustom = 50
  matchOuter = false
  offset = 0
  thread = false
  type = 35
FEATURE [Part::FeaturePython] Screw014  label="M4x50-Screw002"  # Fasteners workbench fastener (typed FeaturePython)
  Placement = pos=(-138.5,-9.52628,39) rot=(-0.652223,0.758027,0;3.14159rad)
  baseObject = -> b_J2_coupler_modified_001_ [Edge29]
  diameter = 6
  invert = false
  length = 12
  lengthCustom = 50
  matchOuter = false
  offset = 0
  thread = false
  type = 35
FEATURE [Part::FeaturePython] Screw015  label="M4x50-Screw003"  # Fasteners workbench fastener (typed FeaturePython)
  Placement = pos=(-134.474,5.5,39) rot=(-0.652223,0.758027,0;3.14159rad)
  baseObject = -> b_J2_coupler_modified_001_ [Edge18]
  diameter = 6
  invert = false
  length = 12
  lengthCustom = 50
  matchOuter = false
  offset = 0
  thread = false
  type = 35
FEATURE [Part::FeaturePython] Screw016  label="M4x20-Screw"  # Fasteners workbench fastener (typed FeaturePython)
  Placement = pos=(-116.937,-15.625,33) rot=(1,0,0;3.14159rad)
  baseObject = -> b_Arm2_modified_001_ [Edge93]
  diameter = 6
  invert = false
  length = 7
  lengthCustom = 20
  matchOuter = false
  offset = 0
  thread = false
  type = 34
FEATURE [Part::FeaturePython] Screw017  label="M4x20-Screw001"  # Fasteners workbench fastener (typed FeaturePython)
  Placement = pos=(-144,-31.25,33) rot=(1,0,0;3.14159rad)
  baseObject = -> b_Arm2_modified_001_ [Edge89]
  diameter = 6
  invert = false
  length = 7
  lengthCustom = 20
  matchOuter = false
  offset = 0
  thread = false
  type = 34
FEATURE [Part::FeaturePython] Screw018  label="M4x20-Screw002"  # Fasteners workbench fastener (typed FeaturePython)
  Placement = pos=(-171.063,-15.625,33) rot=(1,0,0;3.14159rad)
  baseObject = -> b_Arm2_modified_001_ [Edge91]
  diameter = 6
  invert = false
  length = 7
  lengthCustom = 20
  matchOuter = false
  offset = 0
  thread = false
  type = 34
FEATURE [Part::FeaturePython] Screw019  label="M4x20-Screw003"  # Fasteners workbench fastener (typed FeaturePython)
  Placement = pos=(-171.063,15.625,33) rot=(1,0,0;3.14159rad)
  baseObject = -> b_Arm2_modified_001_ [Edge94]
  diameter = 6
  invert = false
  length = 7
  lengthCustom = 20
  matchOuter = false
  offset = 0
  thread = false
  type = 34
FEATURE [Part::FeaturePython] Screw020  label="M4x20-Screw004"  # Fasteners workbench fastener (typed FeaturePython)
  Placement = pos=(-144,31.25,33) rot=(1,0,0;3.14159rad)
  baseObject = -> b_Arm2_modified_001_ [Edge98]
  diameter = 6
  invert = false
  length = 7
  lengthCustom = 20
  matchOuter = false
  offset = 0
  thread = false
  type = 34
FEATURE [Part::FeaturePython] Screw021  label="M4x20-Screw005"  # Fasteners workbench fastener (typed FeaturePython)
  Placement = pos=(-116.937,15.625,33) rot=(1,0,0;3.14159rad)
  baseObject = -> b_Arm2_modified_001_ [Edge105]
  diameter = 6
  invert = false
  length = 7
  lengthCustom = 20
  matchOuter = false
  offset = 0
  thread = false
  type = 34
FEATURE [Part::FeaturePython] Washer  label="M3-Washer"  # Fasteners workbench fastener (typed FeaturePython)
  Placement = pos=(-165.5,15.5,10) rot=(0,0,1;0rad)
  baseObject = -> b_Arm2_cover_modified_001_ [Edge92]
  diameter = 4
  invert = false
  matchOuter = false
  offset = 0
  type = 3
FEATURE [Part::FeaturePython] Washer001  label="M3-Washer001"  # Fasteners workbench fastener (typed FeaturePython)
  Placement = pos=(-165.5,-15.5,10) rot=(0,0,1;0rad)
  baseObject = -> b_Arm2_cover_modified_001_ [Edge115]
  diameter = 4
  invert = false
  matchOuter = false
  offset = 0
  type = 3
FEATURE [Part::FeaturePython] Washer002  label="M3-Washer002"  # Fasteners workbench fastener (typed FeaturePython)
  Placement = pos=(-134.5,15.5,10) rot=(0,0,1;0rad)
  baseObject = -> b_Arm2_cover_modified_001_ [Edge96]
  diameter = 4
  invert = false
  matchOuter = false
  offset = 0
  type = 3
FEATURE [Part::FeaturePython] Washer003  label="M3-Washer003"  # Fasteners workbench fastener (typed FeaturePython)
  Placement = pos=(-134.5,-15.5,10) rot=(0,0,1;0rad)
  baseObject = -> b_Arm2_cover_modified_001_ [Edge119]
  diameter = 4
  invert = false
  matchOuter = false
  offset = 0
  type = 3
FEATURE [Part::FeaturePython] Screw022  label="M3x16-Screw"  # Fasteners workbench fastener (typed FeaturePython)
  Placement = pos=(-165.5,15.5,10.55) rot=(0,0,1;0rad)
  baseObject = -> Washer [Edge1]
  diameter = 4
  invert = false
  length = 7
  lengthCustom = 16
  matchOuter = false
  offset = 0
  thread = false
  type = 34
FEATURE [Part::FeaturePython] Screw023  label="M3x16-Screw001"  # Fasteners workbench fastener (typed FeaturePython)
  Placement = pos=(-165.5,-15.5,10.55) rot=(0,0,1;0rad)
  baseObject = -> Washer001 [Edge1]
  diameter = 4
  invert = false
  length = 7
  lengthCustom = 16
  matchOuter = false
  offset = 0
  thread = false
  type = 34
FEATURE [Part::FeaturePython] Screw024  label="M3x16-Screw002"  # Fasteners workbench fastener (typed FeaturePython)
  Placement = pos=(-134.5,-15.5,10.55) rot=(0,0,1;0rad)
  baseObject = -> Washer003 [Edge1]
  diameter = 4
  invert = false
  length = 7
  lengthCustom = 16
  matchOuter = false
  offset = 0
  thread = false
  type = 34
FEATURE [Part::FeaturePython] Screw025  label="M3x16-Screw003"  # Fasteners workbench fastener (typed FeaturePython)
  Placement = pos=(-134.5,15.5,10.55) rot=(0,0,1;0rad)
  baseObject = -> Washer002 [Edge1]
  diameter = 4
  invert = false
  length = 7
  lengthCustom = 16
  matchOuter = false
  offset = 0
  thread = false
  type = 34
FEATURE [App::DocumentObjectGroup] Group
FEATURE [Part::FeaturePython] b_Pulley_GT2_90t_j3_modified_001_  label="Pulley_GT2_90t_j3_modified_001"  # a2plus imported part (geometry in sourceFile) (typed FeaturePython)
  Placement = pos=(-7.5,-3.39384e-08,18.2) rot=(-0.487845,0.872931,0;3.14159rad)
  a2p_Version = V0.1
  fixedPosition = false
  objectType = a2pPart
  sourceFile = ./Pulley_GT2_90t_j3_modified.FCStd
  subassemblyImport = false
  timeLastImport = 1.62058e+09
  updateColors = true
FEATURE [Part::FeaturePython] Nut018  label="M4-Nut026"  # Fasteners workbench fastener (typed FeaturePython)
  Placement = pos=(1.8688,-5.76417,20.4) rot=(-0.568612,0.822606,0;0rad)
  baseObject = -> b_Pulley_GT2_90t_j3_modified_001_ [Edge117]
  diameter = 2
  invert = false
  matchOuter = false
  offset = 0
  thread = false
  type = 5
FEATURE [Part::FeaturePython] Nut019  label="M4-Nut025"  # Fasteners workbench fastener (typed FeaturePython)
  Placement = pos=(-1.73583,9.3688,20.4) rot=(-0.568612,0.822606,0;0rad)
  baseObject = -> b_Pulley_GT2_90t_j3_modified_001_ [Edge118]
  diameter = 2
  invert = false
  matchOuter = false
  offset = 0
  thread = false
  type = 5
FEATURE [Part::FeaturePython] Nut020  label="M4-Nut024"  # Fasteners workbench fastener (typed FeaturePython)
  Placement = pos=(-16.8688,5.76417,20.4) rot=(-0.568612,0.822606,0;0rad)
  baseObject = -> b_Pulley_GT2_90t_j3_modified_001_ [Edge116]
  diameter = 2
  invert = false
  matchOuter = false
  offset = 0
  thread = false
  type = 5
FEATURE [Part::FeaturePython] Nut021  label="M4-Nut023"  # Fasteners workbench fastener (typed FeaturePython)
  Placement = pos=(-13.2642,-9.3688,20.4) rot=(-0.568612,0.822606,0;0rad)
  baseObject = -> b_Pulley_GT2_90t_j3_modified_001_ [Edge115]
  diameter = 2
  invert = false
  matchOuter = false
  offset = 0
  thread = false
  type = 5
FEATURE [App::FeaturePython] circularEdge_003  label="circularEdge_003__Thrust_bearing_511071_001"  # a2plus constraint (typed FeaturePython)
  Object1 = b_Pulley_GT2_90t_j3_modified_001_
  Object2 = b_Thrust_bearing_511071_001_
  ParentTreeObject = -> b_Pulley_GT2_90t_j3_modified_001_
  SubElement1 = Edge109
  SubElement2 = Edge29
  Suppressed = false
  Type = circularEdge
  directionConstraint = 1
  lockRotation = false
  offset = 0
FEATURE [App::FeaturePython] circularEdge_003_mirror  label="circularEdge_003__Pulley_GT2_90t_j3_modified_001"  # a2plus constraint (typed FeaturePython)
  Object1 = b_Pulley_GT2_90t_j3_modified_001_
  Object2 = b_Thrust_bearing_511071_001_
  ParentTreeObject = -> b_Thrust_bearing_511071_001_
  SubElement1 = Edge109
  SubElement2 = Edge29
  Suppressed = false
  Type = circularEdge
  directionConstraint = 1
  lockRotation = false
  offset = 0
FEATURE [App::FeaturePython] circularEdge_005  label="circularEdge_005__Pulley_GT2_90t_j3_modified_001"  # a2plus constraint (typed FeaturePython)
  Object1 = b_Belt_GT2_400mm_20_901_001_
  Object2 = b_Pulley_GT2_90t_j3_modified_001_
  ParentTreeObject = -> b_Belt_GT2_400mm_20_901_001_
  SubElement1 = Edge8
  SubElement2 = Edge2544
  Suppressed = false
  Type = circularEdge
  directionConstraint = 1
  lockRotation = false
  offset = 0
FEATURE [App::FeaturePython] circularEdge_005_mirror  label="circularEdge_005__Belt_GT2_400mm_20-901_001"  # a2plus constraint (typed FeaturePython)
  Object1 = b_Belt_GT2_400mm_20_901_001_
  Object2 = b_Pulley_GT2_90t_j3_modified_001_
  ParentTreeObject = -> b_Pulley_GT2_90t_j3_modified_001_
  SubElement1 = Edge8
  SubElement2 = Edge2544
  Suppressed = false
  Type = circularEdge
  directionConstraint = 1
  lockRotation = false
  offset = 0
FEATURE [Spreadsheet::Sheet] Fasteners_BOM
  cells = A1=Type; B1=Qty; A2=DIN985 Nut M3; B2=2; A3=DIN985 Nut M4; B3=4; A4=ISO4032 Nut M4; B4=16; A5=ISO7045 Screw M3x16; B5=4; A6=ISO7045 Screw M3x20; B6=2; A7=ISO7045 Screw M4x20; B7=6; A8=ISO7046 Screw M4x25; B8=10; A9=ISO7046 Screw M4x50; B9=4; A10=ISO7089 Washer M3; B10=4
FEATURE [Spreadsheet::Sheet] _PARTSLIST_  label="#PARTSLIST#"
  cells = A1=POS; B1=QTY; C1=IDENTNO; D1=DESCRIPTION; E1=SUPPLIER; F1=SUPP.IDENTNO; G1=SUPP.DESCRIPTION; H1=(FILENAME); A2=1; B2=1; C2=*; D2=*; E2=*; F2=*; G2=*; H2=Arm2_cover_modified.FCStd; A3=2; B3=2; C3=*; D3=*; E3=*; F3=*; G3=*; H3=Thrust_bearing_51107.step; A4=3; B4=1; C4=*; D4=*; E4=*; F4=*; G4=*; H4=Stepper_NEMA17_l24mm_shaft_20mm.step; A5=4; B5=1; C5=*; D5=*; E5=*; F5=*; G5=*; H5=Pulley_GT2-20t.step; A6=5; B6=1; C6=*; D6=*; E6=*; F6=*; G6=*; H6=Belt_GT2_400mm_20-90.step; A7=6; B7=1; C7=*; D7=*; E7=*; F7=*; G7=*; H7=Arm2_modified.FCStd; A8=7; B8=3; C8=*; D8=*; E8=*; F8=*; G8=*; H8=Cable_routing_clamp_16*8*4.5.FCStd; A9=8; B9=1; C9=*; D9=*; E9=*; F9=*; G9=*; H9=J2_coupler_modified.FCStd; A10=9; B10=1; C10=*; D10=*; E10=*; F10=*; G10=*; H10=Switch_endstop.step; A11=10; B11=1; C11=*; D11=*; E11=*; F11=*; G11=*; H11=Pulley_GT2_90t_j3_modified.FCStd; A12=11; B12=1; C12=*; D12=*; E12=*; F12=*; G12=*; H12=Ball_bearing_6806.step
FEATURE [Part::FeaturePython] b_Ball_bearing_68061_001_  label="Ball_bearing_68061_001"  # a2plus imported part (geometry in sourceFile) (typed FeaturePython)
  Placement = pos=(-7.5,0,1) rot=(1,0,0;1.5708rad)
  a2p_Version = V0.1
  fixedPosition = false
  muxInfo = <blob: 2407 chars omitted>
  objectType = a2pPart
  sourceFile = ./Ball_bearing_6806.step
  subassemblyImport = false
  timeLastImport = 1.62074e+09
  updateColors = true
FEATURE [App::FeaturePython] circularEdge_001  label="circularEdge_001__Arm2_cover_modified_001"  # a2plus constraint (typed FeaturePython)
  Object1 = b_Ball_bearing_68061_001_
  Object2 = b_Arm2_cover_modified_001_
  ParentTreeObject = -> b_Ball_bearing_68061_001_
  SubElement1 = Edge21
  SubElement2 = Edge265
  Suppressed = false
  Type = circularEdge
  directionConstraint = 0
  lockRotation = false
  offset = 0
FEATURE [App::FeaturePython] circularEdge_001_mirror  label="circularEdge_001__Ball_bearing_68061_001"  # a2plus constraint (typed FeaturePython)
  Object1 = b_Ball_bearing_68061_001_
  Object2 = b_Arm2_cover_modified_001_
  ParentTreeObject = -> b_Arm2_cover_modified_001_
  SubElement1 = Edge21
  SubElement2 = Edge265
  Suppressed = false
  Type = circularEdge
  directionConstraint = 0
  lockRotation = false
  offset = 0
